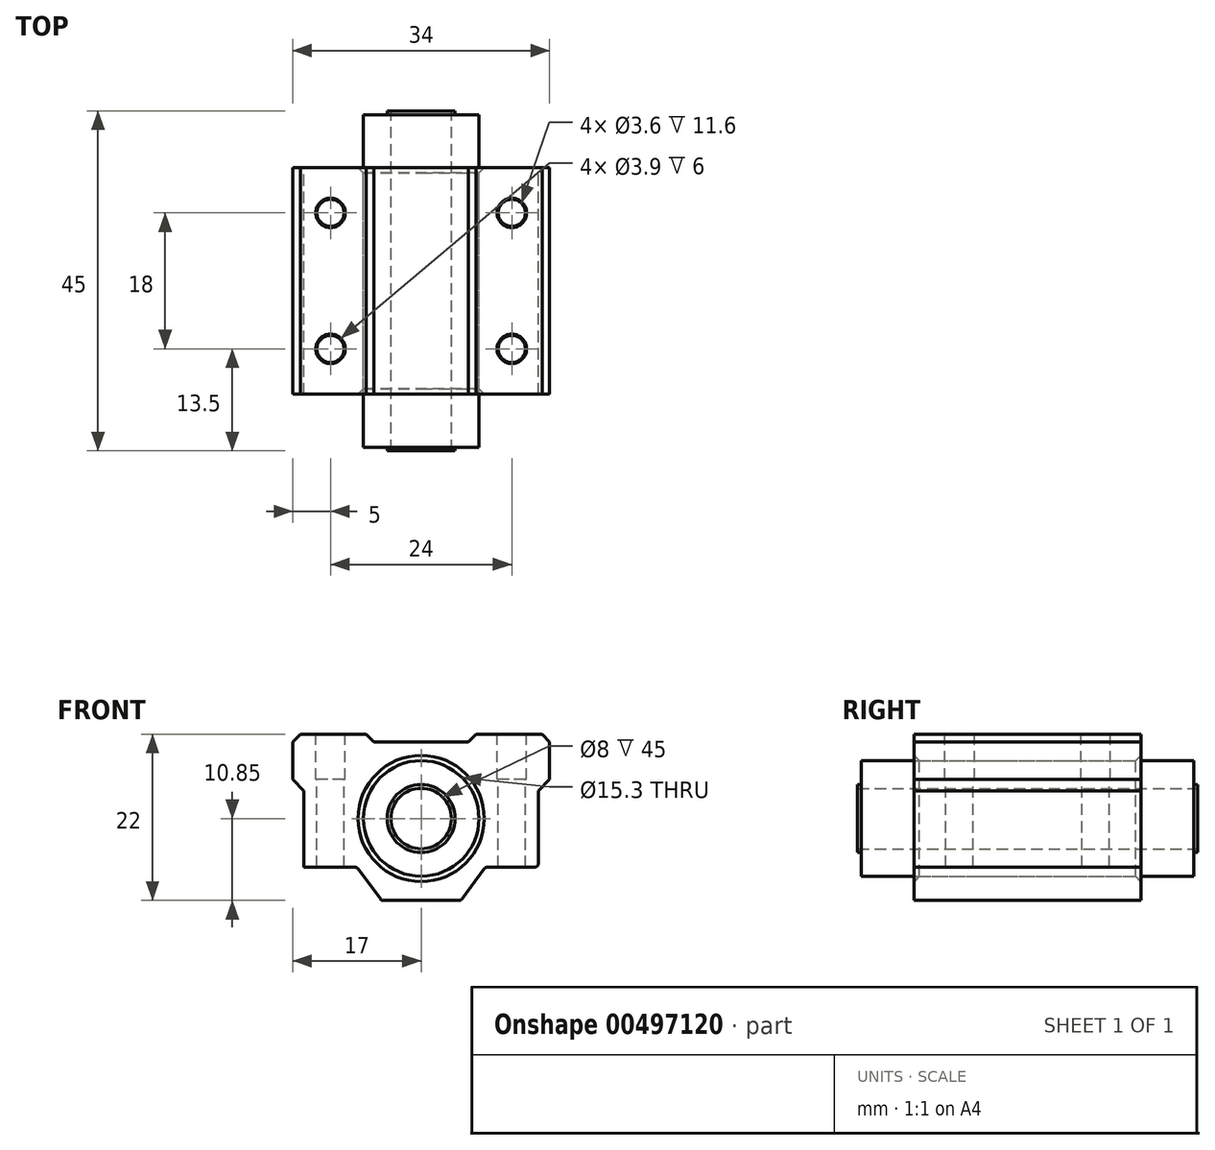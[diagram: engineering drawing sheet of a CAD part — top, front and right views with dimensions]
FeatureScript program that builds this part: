
annotation { "Feature Type Name" : "Feature", "Feature Type Description" : "" }
export const myFeature = defineFeature(function(context is Context, id is Id, definition is map)
    precondition{}
    {
        {
            var Q0;
            Q0=qCreatedBy(makeId("Front.planeOp"),FACE);
            var sketch = newSketch(context, id + "F0", { "sketchPlane" : qUnion([Q0])});
            skCircle(sketch, "E0", {"center": v(0, 0) * mm, "radius": 4 * mm});
            skCircle(sketch, "E1", {"center": v(0, 0) * mm, "radius": 7.65 * mm});
            skLineSegment(sketch, "E2", {"start": v(0, 0) * mm, "end": v(0, 22.9) * mm, "construction": true});
            skLineSegment(sketch, "E3", {"start": v(0, 7.65) * mm, "end": v(0, 10.15) * mm});
            skLineSegment(sketch, "E4", {"start": v(0, 10.15) * mm, "end": v(7.25, 10.15) * mm});
            skLineSegment(sketch, "E5", {"start": v(7.25, 10.15) * mm, "end": v(7.25, 11.15) * mm});
            skLineSegment(sketch, "E6", {"start": v(7.25, 11.15) * mm, "end": v(17, 11.15) * mm});
            skLineSegment(sketch, "E7", {"start": v(17, 11.15) * mm, "end": v(17, 3.65) * mm});
            skLineSegment(sketch, "E8", {"start": v(17, 3.65) * mm, "end": v(15.5, 3.65) * mm});
            skLineSegment(sketch, "E9", {"start": v(15.5, 3.65) * mm, "end": v(15.5, -6.45) * mm});
            skLineSegment(sketch, "E10", {"start": v(15.5, -6.45) * mm, "end": v(8.5, -6.45) * mm});
            skLineSegment(sketch, "E11", {"start": v(8.5, -6.45) * mm, "end": v(5.25, -10.85) * mm});
            skLineSegment(sketch, "E12", {"start": v(5.25, -10.85) * mm, "end": v(0, -10.85) * mm});
            skLineSegment(sketch, "E13", {"start": v(0, -10.85) * mm, "end": v(0, -7.65) * mm});
            skCircle(sketch, "E14", {"center": v(0, 0) * mm, "radius": 4.5 * mm});
            skLineSegment(sketch, "E15.MirrorCS", {"start": v(-5.25, -10.85) * mm, "end": v(0, -10.85) * mm});
            skLineSegment(sketch, "E16.MirrorCS", {"start": v(-8.5, -6.45) * mm, "end": v(-5.25, -10.85) * mm});
            skLineSegment(sketch, "E17.MirrorCS", {"start": v(-17, 3.65) * mm, "end": v(-15.5, 3.65) * mm});
            skLineSegment(sketch, "E18.MirrorCS", {"start": v(-17, 11.15) * mm, "end": v(-17, 3.65) * mm});
            skLineSegment(sketch, "E19.MirrorCS", {"start": v(-7.25, 11.15) * mm, "end": v(-17, 11.15) * mm});
            skLineSegment(sketch, "E20.MirrorCS", {"start": v(-7.25, 10.15) * mm, "end": v(-7.25, 11.15) * mm});
            skLineSegment(sketch, "E21.MirrorCS", {"start": v(0, 10.15) * mm, "end": v(-7.25, 10.15) * mm});
            skLineSegment(sketch, "E22", {"start": v(-15.5, 3.65) * mm, "end": v(-15.5, -6.45) * mm});
            skLineSegment(sketch, "E23", {"start": v(-15.5, -6.45) * mm, "end": v(-8.5, -6.45) * mm});
            skSolve(sketch);
        }
        {
            var Q0;
            {var subQ0=sQuery(id+"F0.wireOp",EDGE,"E3");Q0=makeQuery(id+"F0.imprint","IMPRINT",FACE,{"disambiguationData":[TD([[makeQuery(id+"F0.imprint","IMPRINT",EDGE,{"derivedFrom":subQ0}),-1.0]])]});}
            var Q1;
            {var subQ0=sQuery(id+"F0.wireOp",EDGE,"E3");Q1=makeQuery(id+"F0.imprint","IMPRINT",FACE,{"disambiguationData":[TD([[makeQuery(id+"F0.imprint","IMPRINT",EDGE,{"derivedFrom":subQ0}),1.0]])]});}
            extrude(context, id + "F1", {"entities" : qUnion([Q0, Q1]), "depth" : 30 * mm, "offsetDistance" : 25 * mm, "symmetric" : true});
        }
        {
            var Q0;
            Q0=makeQuery(id+"F1.opExtrude","SWEPT_EDGE",EDGE,{"disambiguationData":[OSD([sQuery(id+"F0.wireOp",EDGE,"E4"),sQuery(id+"F0.wireOp",EDGE,"E5")])]});
            var Q1;
            Q1=makeQuery(id+"F1.opExtrude","SWEPT_EDGE",EDGE,{"disambiguationData":[OSD([sQuery(id+"F0.wireOp",EDGE,"E6"),sQuery(id+"F0.wireOp",EDGE,"E7")])]});
            var Q2;
            Q2=makeQuery(id+"F1.opExtrude","SWEPT_EDGE",EDGE,{"disambiguationData":[OSD([sQuery(id+"F0.wireOp",EDGE,"E20.MirrorCS"),sQuery(id+"F0.wireOp",EDGE,"E21.MirrorCS")])]});
            var Q3;
            Q3=makeQuery(id+"F1.opExtrude","SWEPT_EDGE",EDGE,{"disambiguationData":[OSD([sQuery(id+"F0.wireOp",EDGE,"E18.MirrorCS"),sQuery(id+"F0.wireOp",EDGE,"E19.MirrorCS")])]});
            chamfer(context, id + "F2", {"entities" : qUnion([Q0, Q1, Q2, Q3]), "width" : 1 * mm, "tangentPropagation" : true});
        }
        {
            var Q0;
            Q0=makeQuery(id+"F1.opExtrude","SWEPT_EDGE",EDGE,{"disambiguationData":[OSD([sQuery(id+"F0.wireOp",EDGE,"E7"),sQuery(id+"F0.wireOp",EDGE,"E8")])]});
            var Q1;
            Q1=makeQuery(id+"F1.opExtrude","SWEPT_EDGE",EDGE,{"disambiguationData":[OSD([sQuery(id+"F0.wireOp",EDGE,"E17.MirrorCS"),sQuery(id+"F0.wireOp",EDGE,"E18.MirrorCS")])]});
            chamfer(context, id + "F3", {"entities" : qUnion([Q0, Q1]), "width" : 1.5 * mm, "tangentPropagation" : true});
        }
        {
            var Q0;
            Q0=makeQuery(id+"F1.opExtrude","SWEPT_EDGE",EDGE,{"disambiguationData":[OSD([sQuery(id+"F0.wireOp",EDGE,"E9"),sQuery(id+"F0.wireOp",EDGE,"E10")])]});
            var Q1;
            Q1=makeQuery(id+"F1.opExtrude","SWEPT_EDGE",EDGE,{"disambiguationData":[OSD([sQuery(id+"F0.wireOp",EDGE,"E10"),sQuery(id+"F0.wireOp",EDGE,"E11")])]});
            var Q2;
            Q2=makeQuery(id+"F1.opExtrude","SWEPT_EDGE",EDGE,{"disambiguationData":[OSD([sQuery(id+"F0.wireOp",EDGE,"E11"),sQuery(id+"F0.wireOp",EDGE,"E12")])]});
            var Q3;
            Q3=makeQuery(id+"F1.opExtrude","SWEPT_EDGE",EDGE,{"disambiguationData":[OSD([sQuery(id+"F0.wireOp",EDGE,"E15.MirrorCS"),sQuery(id+"F0.wireOp",EDGE,"E16.MirrorCS")])]});
            var Q4;
            Q4=makeQuery(id+"F1.opExtrude","SWEPT_EDGE",EDGE,{"disambiguationData":[OSD([sQuery(id+"F0.wireOp",EDGE,"E16.MirrorCS"),sQuery(id+"F0.wireOp",EDGE,"O6NMc8kR-GBqP-20ma-tIkf-TSFbQtPsBvN1")])]});
            fillet(context, id + "F4", {"entities" : qUnion([Q0, Q1, Q2, Q3, Q4]), "radius" : .5 * mm, "tangentPropagation" : true, "allowEdgeOverflow" : false});
        }
        {
            var Q0;
            Q0=makeQuery(id+"F1.opExtrude","SWEPT_FACE",FACE,{"disambiguationData":[OSD([sQuery(id+"F0.wireOp",EDGE,"E6")])]});
            var sketch = newSketch(context, id + "F5", { "sketchPlane" : qUnion([Q0])});
            skLineSegment(sketch, "E24.bottom", {"start": v(-12, 9) * mm, "end": v(12, 9) * mm});
            skLineSegment(sketch, "E24.top", {"start": v(-12, -9) * mm, "end": v(12, -9) * mm});
            skLineSegment(sketch, "E24.left", {"start": v(-12, 9) * mm, "end": v(-12, -9) * mm});
            skLineSegment(sketch, "E24.right", {"start": v(12, 9) * mm, "end": v(12, -9) * mm});
            skLineSegment(sketch, "E25", {"start": v(-12, 9) * mm, "end": v(12, -9) * mm});
            skSolve(sketch);
        }
        {
            var Q0;
            Q0=sQuery(id+"F5.wireOp",VERTEX,"E24.right.start");
            var Q1;
            Q1=sQuery(id+"F5.wireOp",VERTEX,"E25.end");
            var Q2;
            Q2=sQuery(id+"F5.wireOp",VERTEX,"E25.start");
            var Q3;
            Q3=sQuery(id+"F5.wireOp",VERTEX,"E24.left.end");
            var Q4;
            Q4=makeQuery(id+"F1.opExtrude","SWEPT_BODY",BODY,{"disambiguationData":[OSD([sQuery(id+"F0.wireOp",EDGE,"E1"),sQuery(id+"F0.wireOp",EDGE,"E3"),sQuery(id+"F0.wireOp",EDGE,"E4"),sQuery(id+"F0.wireOp",EDGE,"E5"),sQuery(id+"F0.wireOp",EDGE,"E6"),sQuery(id+"F0.wireOp",EDGE,"E7"),sQuery(id+"F0.wireOp",EDGE,"E8"),sQuery(id+"F0.wireOp",EDGE,"E9"),sQuery(id+"F0.wireOp",EDGE,"E10"),sQuery(id+"F0.wireOp",EDGE,"E11"),sQuery(id+"F0.wireOp",EDGE,"E12"),sQuery(id+"F0.wireOp",EDGE,"E13")])]});
            hole(context, id + "F6", {"style" : HoleStyle.C_BORE, "endStyle" : HoleEndStyle.THROUGH, "holeDiameter" : 3.6 * mm, "cBoreDiameter" : 3.9 * mm, "cBoreDepth" : 6 * mm, "locations" : qUnion([Q0, Q1, Q2, Q3]), "scope" : qUnion([Q4]), "tappedDepth" : 12 * mm, "tapClearance" : 3});
        }
        {
            var Q0;
            Q0=makeQuery(id+"F6.hole-1.boolean.opBoolean","COPY",EDGE,{"derivedFrom":makeQuery(id+"F6.hole-1.opRevolve","SWEPT_EDGE",EDGE,{"disambiguationData":[OSD([sQuery(id+"F6.hole-1.sketch.wireOp",EDGE,"cbore_start_line_2"),sQuery(id+"F6.hole-1.sketch.wireOp",EDGE,"cbore_start_line_3")])]})});
            var Q1;
            Q1=makeQuery(id+"F6.hole-0.boolean.opBoolean","COPY",EDGE,{"derivedFrom":makeQuery(id+"F6.hole-0.opRevolve","SWEPT_EDGE",EDGE,{"disambiguationData":[OSD([sQuery(id+"F6.hole-0.sketch.wireOp",EDGE,"cbore_start_line_2"),sQuery(id+"F6.hole-0.sketch.wireOp",EDGE,"cbore_start_line_3")])]})});
            var Q2;
            Q2=makeQuery(id+"F1.opExtrude","CAP_EDGE",EDGE,{"disambiguationData":[OSD([sQuery(id+"F0.wireOp",EDGE,"E1")])],"isStart":false});
            var Q3;
            Q3=makeQuery(id+"F1.opExtrude","CAP_EDGE",EDGE,{"disambiguationData":[OSD([sQuery(id+"F0.wireOp",EDGE,"E1")])],"isStart":true});
            var Q4;
            Q4=makeQuery(id+"F6.hole-3.boolean.opBoolean","COPY",EDGE,{"derivedFrom":makeQuery(id+"F6.hole-3.opRevolve","SWEPT_EDGE",EDGE,{"disambiguationData":[OSD([sQuery(id+"F6.hole-3.sketch.wireOp",EDGE,"cbore_start_line_2"),sQuery(id+"F6.hole-3.sketch.wireOp",EDGE,"cbore_start_line_3")])]})});
            var Q5;
            Q5=makeQuery(id+"F6.hole-2.boolean.opBoolean","COPY",EDGE,{"derivedFrom":makeQuery(id+"F6.hole-2.opRevolve","SWEPT_EDGE",EDGE,{"disambiguationData":[OSD([sQuery(id+"F6.hole-2.sketch.wireOp",EDGE,"cbore_start_line_2"),sQuery(id+"F6.hole-2.sketch.wireOp",EDGE,"cbore_start_line_3")])]})});
            chamfer(context, id + "F7", {"entities" : qUnion([Q0, Q1, Q2, Q3, Q4, Q5]), "width" : .7 * mm, "tangentPropagation" : true});
        }
        {
            var Q0;
            Q0=makeQuery(id+"F0.imprint","IMPRINT",FACE,{"disambiguationData":[TD([[makeQuery(id+"F0.imprint","IMPRINT",EDGE,{"derivedFrom":sQuery(id+"F0.wireOp",EDGE,"E14")}),-1.0]])]});
            extrude(context, id + "F8", {"entities" : qUnion([Q0]), "depth" : 44 * mm, "symmetric" : true});
        }
        {
            var Q0;
            Q0=makeQuery(id+"F0.imprint","IMPRINT",FACE,{"disambiguationData":[TD([[makeQuery(id+"F0.imprint","IMPRINT",EDGE,{"derivedFrom":sQuery(id+"F0.wireOp",EDGE,"E0")}),-1.0]])]});
            extrude(context, id + "F9", {"entities" : qUnion([Q0]), "operationType" : NewBodyOperationType.ADD, "depth" : 45 * mm, "symmetric" : true});
        }
    });
